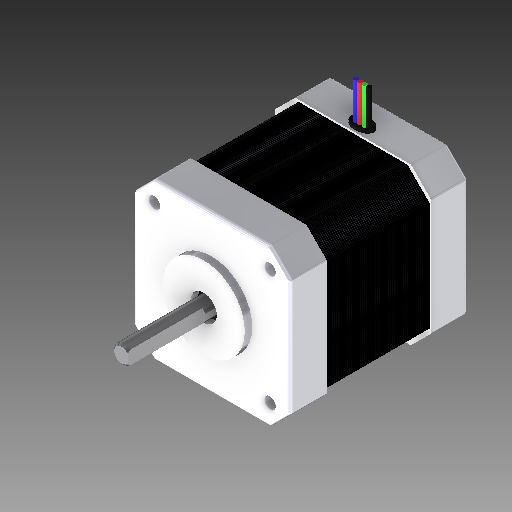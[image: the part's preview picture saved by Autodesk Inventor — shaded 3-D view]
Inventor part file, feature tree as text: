
AUTODESK INVENTOR PART (.ipt)
format: ipt  version: 2017 (Build 210142000, 142)  size: 1,185,792 bytes
history: native  units: mm
features: extrude x13, sketch x5, hole x4, fillet x4, chamfer x2, plane x1, pattern_linear x1, projected_geometry x1
ambient origin geometry x8: Origin, YZ Plane, XZ Plane, XY Plane, X Axis, Y Axis, Z Axis, Center Point
bodies: Solid1 (feature_tree)
feature tree (31):
  sketch  "Sketch1"  dims[d0=7.0mm d1=22.0mm]
  extrude  "Extrusion1"  Depth=22.0mm
  extrude  "Extrusion2"  Depth=31.0mm
  extrude  "Extrusion3"  Depth=3.0mm
  plane  "Work Plane2"
  extrude  "Extrusion7"  Depth=3.0mm
  extrude  "Extrusion8"  Depth=10.0mm
  chamfer  "Chamfer1"  Distance=42.0mm
  pattern_linear  "Rectangular Pattern2"  Spacing1=135.0deg  [1 undecoded]
  hole  "Hole1"  [1 undecoded]
  hole  "Hole2"  [1 undecoded]
  hole  "Hole3"  [1 undecoded]
  hole  "Hole4"  [1 undecoded]
  extrude  "Extrusion9"  Depth=10.0mm TaperAngle=0.0deg
  fillet  "Fillet1"  Radius=2.0mm
  fillet  "Fillet2"  Radius=48.0mm
  chamfer  "Chamfer2"  [1 undecoded]
  fillet  "Fillet3"  Radius=28.0mm
  sketch  "Sketch6"  dims[d10=3.0mm d11=3.0mm]
  extrude  "Extrusion10"  Depth=10.0mm
  fillet  "Fillet4"  Radius=1.0mm
  extrude  "Extrusion11"  Depth=10.0mm
  extrude  "Extrusion12"  Depth=10.0mm
  extrude  "Extrusion13"  Depth=10.0mm
  extrude  "Extrusion14"  Depth=10.0mm
  extrude  "Extrusion15"  Depth=10.0mm
  extrude  "Extrusion16"  Depth=10.0mm
  sketch  "Sketch4"  dims[d4=5.0mm d5=31.0mm]
  projected_geometry  "Projected Loop2"
  sketch  "Sketch5"  dims[d6=31.0mm d9=3.0mm]
  sketch  "Sketch11"  dims[d12=3.0mm d39=42.0mm d40=42.0mm d41=135.0deg d42=51.618795mm d43=51.618795mm d44=25.809398mm d45=25.809398mm d46=24.0mm d47=0.0mm d48=2.0mm d49=0.0mm d50=48.0mm d51=0.0mm d60=-10.0mm d126=28.0mm d127=0.0mm d128=1.0mm d129=1.0mm d130=1.0mm d131=1.0mm d132=0.5mm d134=0.5mm d135=0.5mm d136=0.5mm d137=0.5mm d138=1.0mm d139=1.0mm d140=0.5mm d141=0.0mm d145=0.125mm d146=2.0mm d147=45.0deg d148=560.0mm d150=0.5mm d151=10.0mm d152=10.0mm d153=6.0mm d154=6.0mm d155=4.0mm d156=2.0mm d157=90.0deg d158=3.0mm d159=0.0mm d160=10.0mm d161=10.0mm d162=6.0mm d163=6.0mm d164=4.0mm d165=2.0mm d166=90.0deg d167=3.0mm d168=0.0mm d169=10.0mm d170=10.0mm d171=6.0mm d172=6.0mm d173=4.0mm d174=2.0mm d175=90.0deg d176=3.0mm d177=0.0mm d178=10.0mm d179=10.0mm d180=6.0mm d181=6.0mm d182=4.0mm d183=2.0mm d184=90.0deg d185=3.0mm d186=0.0mm d187=48.0mm d188=0.0mm d189=47.0mm d190=0.0mm d191=1.0mm d192=1.0mm d193=0.5mm d194=2.0mm d195=45.0deg d196=0.5mm d197=1.2mm d198=40.0mm d200=1.2mm d201=10.0mm d203=10.0mm d205=2.5mm d206=2.5mm d207=1.0mm d208=0.0mm d209=0.3mm d210=10.0mm d211=0.0mm d212=10.0mm d213=0.0mm d214=10.0mm d215=0.0mm d216=10.0mm d217=0.0mm d218=0.2mm d219=5.0mm d220=0.0mm d221=0.0mm d225=20.0mm d226=0.0mm]
note: 6 required parameter values undecoded (feature->parameter linkage not recoverable at this tier; creation-order binding heuristic only, values carry confidence <= 0.55)
